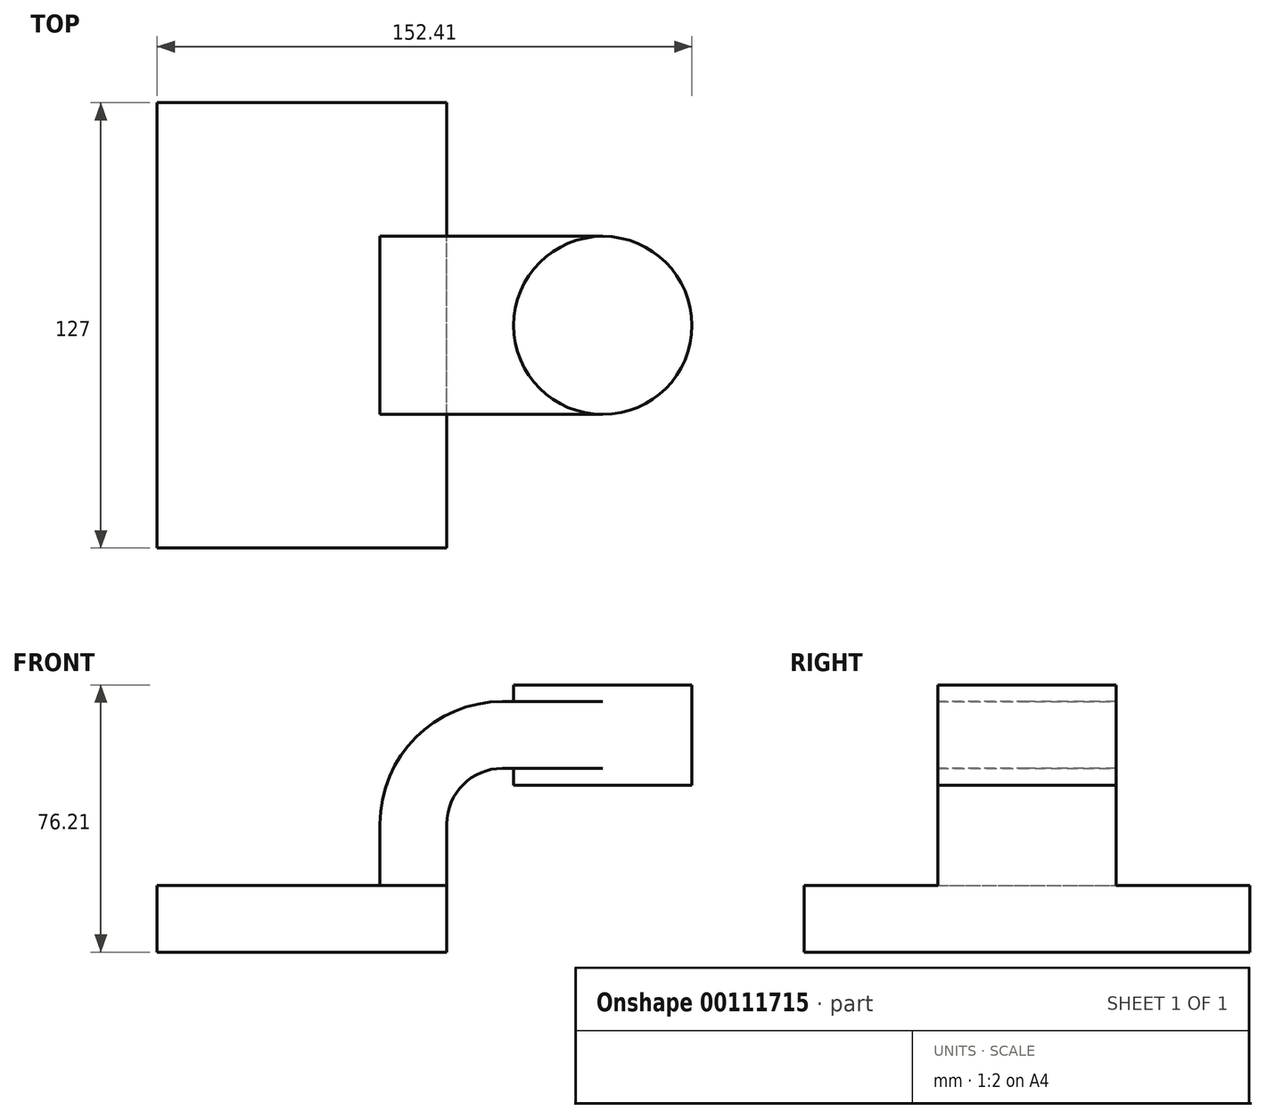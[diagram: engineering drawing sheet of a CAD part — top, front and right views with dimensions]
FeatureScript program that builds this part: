
annotation { "Feature Type Name" : "Feature", "Feature Type Description" : "" }
export const myFeature = defineFeature(function(context is Context, id is Id, definition is map)
    precondition{}
    {
        {
            var Q0;
            Q0=qCreatedBy(makeId("Front.planeOp"),FACE);
            var sketch = newSketch(context, id + "F0", { "sketchPlane" : qUnion([Q0])});
            skLineSegment(sketch, "E0.bottom", {"start": v(41.28, -9.52) * mm, "end": v(-41.27, -9.53) * mm});
            skLineSegment(sketch, "E0.top", {"start": v(41.27, 9.53) * mm, "end": v(-41.28, 9.53) * mm});
            skLineSegment(sketch, "E0.left", {"start": v(41.28, -9.52) * mm, "end": v(41.28, 9.53) * mm});
            skLineSegment(sketch, "E0.right", {"start": v(-41.27, -9.52) * mm, "end": v(-41.28, 9.53) * mm});
            skPoint(sketch, "E0.middle", {"position": v(0, 0) * mm});
            skLineSegment(sketch, "E1.bottom", {"start": v(111.12, 38.1) * mm, "end": v(60.33, 38.1) * mm});
            skLineSegment(sketch, "E1.top", {"start": v(111.12, 66.68) * mm, "end": v(60.33, 66.68) * mm});
            skLineSegment(sketch, "E1.left", {"start": v(111.12, 38.1) * mm, "end": v(111.12, 66.68) * mm});
            skLineSegment(sketch, "E1.right", {"start": v(60.33, 38.1) * mm, "end": v(60.33, 66.68) * mm});
            skPoint(sketch, "E1.middle", {"position": v(85.72, 52.39) * mm});
            skLineSegment(sketch, "E2", {"start": v(41.27, 9.53) * mm, "end": v(41.27, 27) * mm});
            skArc(sketch, "E3", {"start": v(41.27, 27) * mm, "mid": v(45.92, 38.23) * mm, "end": v(57.15, 42.88) * mm});
            skLineSegment(sketch, "E4", {"start": v(57.15, 42.88) * mm, "end": v(85.72, 42.88) * mm});
            skLineSegment(sketch, "E5.0", {"start": v(57.15, 61.93) * mm, "end": v(85.72, 61.93) * mm});
            skArc(sketch, "E5.1", {"start": v(22.23, 27) * mm, "mid": v(32.45, 51.7) * mm, "end": v(57.15, 61.93) * mm});
            skLineSegment(sketch, "E5.2", {"start": v(22.22, 9.53) * mm, "end": v(22.22, 27) * mm});
            skLineSegment(sketch, "E6", {"start": v(85.72, 38.1) * mm, "end": v(85.72, 66.68) * mm});
            skFitSpline(sketch, "E7", {"points": [v(-41.28, 9.53) * mm, v(60.33, 66.68) * mm], "startDerivative": vector(2.64, 52.96) * mm, "endDerivative": vector(168.79, 1.13) * mm});
            skSolve(sketch);
        }
        {
            var Q0;
            Q0=makeQuery(id+"F0.imprint","IMPRINT",FACE,{"disambiguationData":[TD([[makeQuery(id+"F0.imprint","IMPRINT",EDGE,{"derivedFrom":sQuery(id+"F0.wireOp",EDGE,"E0.bottom")}),-1.0]])]});
            extrude(context, id + "F1", {"entities" : qUnion([Q0]), "endBound" : BoundingType.SYMMETRIC, "depth" : 127 * mm});
        }
        {
            var Q0;
            {var subQ1=sQuery(id+"F0.wireOp",EDGE,"E2");Q0=makeQuery(id+"F0.imprint","IMPRINT",FACE,{"disambiguationData":[TD([[makeQuery(id+"F0.imprint","IMPRINT",EDGE,{"derivedFrom":subQ1}),1.0]])]});}
            var Q1;
            {var subQ0=sQuery(id+"F0.wireOp",EDGE,"E4");var subQ1=sQuery(id+"F0.wireOp",EDGE,"E1.right");var subQ2=makeQuery(id+"F0.imprint","INTERSECT",VERTEX,{"derivedFrom":[subQ1,subQ0]});Q1=makeQuery(id+"F0.imprint","IMPRINT",FACE,{"disambiguationData":[TD([[makeQuery(id+"F0.imprint","IMPRINT",EDGE,{"disambiguationData":[TD([[subQ2,-1.0]])],"derivedFrom":subQ1}),-1.0]])]});}
            extrude(context, id + "F2", {"entities" : qUnion([Q0, Q1]), "operationType" : NewBodyOperationType.ADD, "endBound" : BoundingType.SYMMETRIC, "depth" : 50.8 * mm});
        }
        {
            var Q0;
            {var subQ0=sQuery(id+"F0.wireOp",EDGE,"E5.1");Q0=makeQuery(id+"F0.imprint","IMPRINT",FACE,{"disambiguationData":[TD([[makeQuery(id+"F0.imprint","IMPRINT",EDGE,{"derivedFrom":subQ0}),1.0]])]});}
            extrude(context, id + "F3", {"entities" : qUnion([Q0]), "operationType" : NewBodyOperationType.ADD, "endBound" : BoundingType.SYMMETRIC, "depth" : 15.88 * mm});
        }
        {
            var Q0;
            {var subQ0=sQuery(id+"F0.wireOp",EDGE,"E1.left");Q0=makeQuery(id+"F0.imprint","IMPRINT",FACE,{"disambiguationData":[TD([[makeQuery(id+"F0.imprint","IMPRINT",EDGE,{"derivedFrom":subQ0}),1.0]])]});}
            var Q1;
            Q1=sQuery(id+"F0.wireOp",EDGE,"E6");
            revolve(context, id + "F4", {"operationType" : NewBodyOperationType.ADD, "entities" : qUnion([Q0]), "axis" : qUnion([Q1]), "revolveType" : RevolveType.FULL});
        }
        {
            var Q0;
            {var subQ0=sQuery(id+"F0.wireOp",EDGE,"E1.left");Q0=makeQuery(id+"F0.imprint","IMPRINT",FACE,{"disambiguationData":[TD([[makeQuery(id+"F0.imprint","IMPRINT",EDGE,{"derivedFrom":subQ0}),1.0]])]});}
            var Q1;
            Q1=sQuery(id+"F0.wireOp",EDGE,"E6");
            revolve(context, id + "F5", {"operationType" : NewBodyOperationType.ADD, "entities" : qUnion([Q0]), "axis" : qUnion([Q1]), "revolveType" : RevolveType.FULL});
        }
    });
